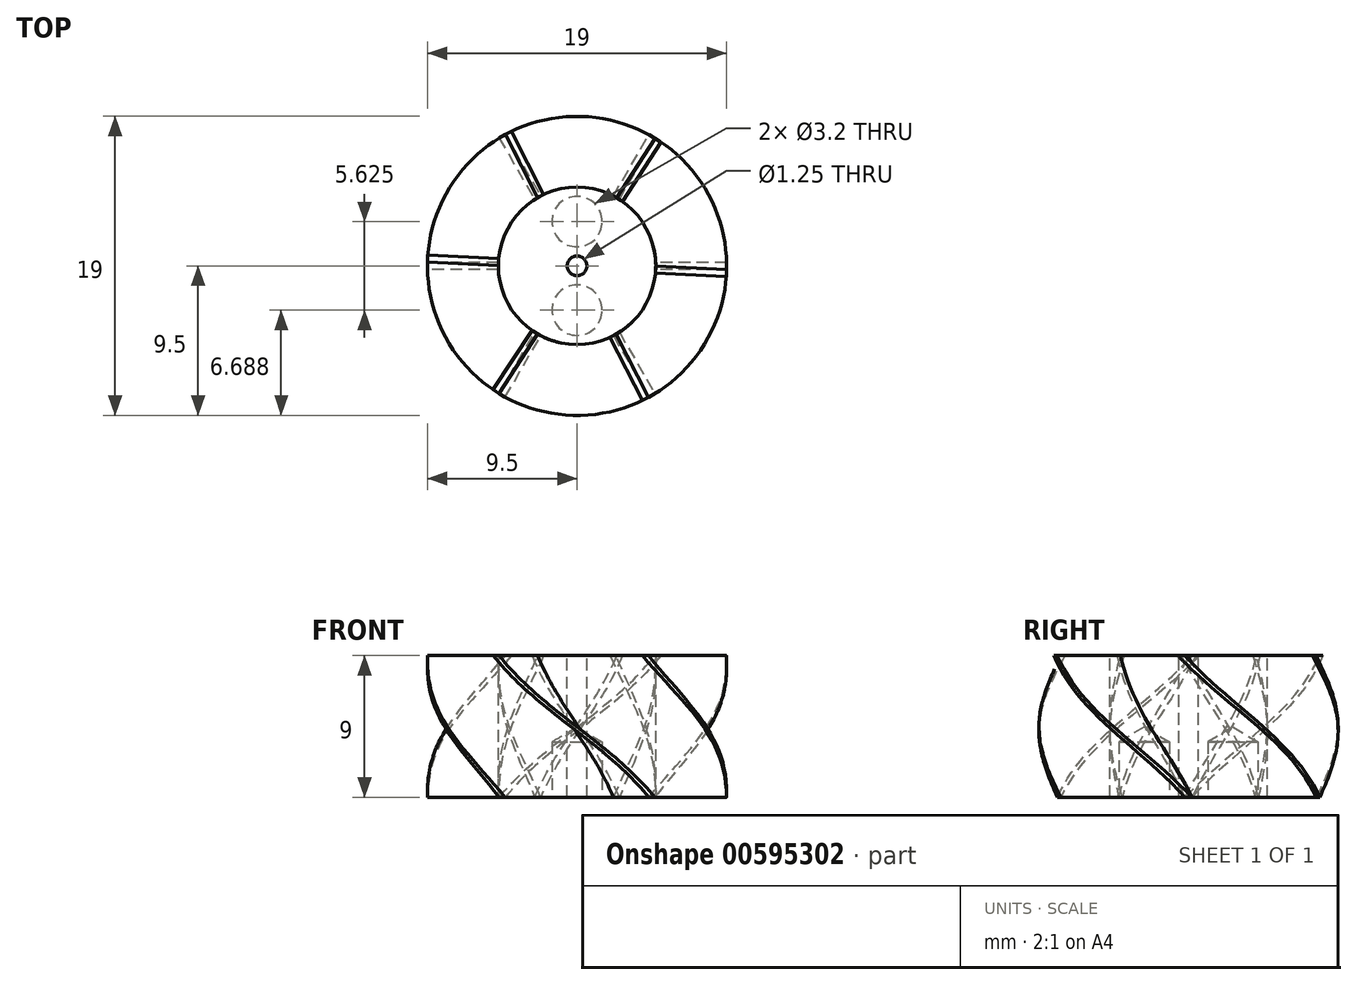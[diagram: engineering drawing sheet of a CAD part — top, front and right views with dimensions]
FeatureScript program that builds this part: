
annotation { "Feature Type Name" : "Feature", "Feature Type Description" : "" }
export const myFeature = defineFeature(function(context is Context, id is Id, definition is map)
    precondition{}
    {
        {
            var Q0;
            Q0=qCreatedBy(makeId("Top.planeOp"),FACE);
            var sketch = newSketch(context, id + "F0", { "sketchPlane" : qUnion([Q0])});
            skCircle(sketch, "E0", {"center": v(0, 0) * mm, "radius": 5 * mm});
            skLineSegment(sketch, "E1.bottom", {"start": v(13, -0.22) * mm, "end": v(5, -0.22) * mm});
            skLineSegment(sketch, "E1.top", {"start": v(13, 0.22) * mm, "end": v(5, 0.22) * mm});
            skLineSegment(sketch, "E1.left", {"start": v(13, -0.22) * mm, "end": v(13, 0.22) * mm});
            skLineSegment(sketch, "E1.right", {"start": v(-13, -0.22) * mm, "end": v(-13, 0.22) * mm});
            skLineSegment(sketch, "E2.1.0", {"start": v(-6.3, 11.36) * mm, "end": v(-6.69, 11.14) * mm});
            skLineSegment(sketch, "E2.1.1", {"start": v(6.69, -11.14) * mm, "end": v(6.3, -11.36) * mm});
            skLineSegment(sketch, "E2.1.2", {"start": v(-6.69, 11.14) * mm, "end": v(-2.69, 4.22) * mm});
            skLineSegment(sketch, "E2.1.3", {"start": v(-6.3, 11.36) * mm, "end": v(-2.3, 4.44) * mm});
            skLineSegment(sketch, "E2.2.0", {"start": v(-6.69, -11.14) * mm, "end": v(-6.3, -11.36) * mm});
            skLineSegment(sketch, "E2.2.1", {"start": v(6.3, 11.36) * mm, "end": v(6.69, 11.14) * mm});
            skLineSegment(sketch, "E2.2.2", {"start": v(-6.3, -11.36) * mm, "end": v(-2.3, -4.44) * mm});
            skLineSegment(sketch, "E2.2.3", {"start": v(-6.69, -11.14) * mm, "end": v(-2.69, -4.22) * mm});
            skLineSegment(sketch, "E3.trimOffspring", {"start": v(2.3, 4.44) * mm, "end": v(6.3, 11.36) * mm});
            skLineSegment(sketch, "E4.trimOffspring", {"start": v(2.69, 4.22) * mm, "end": v(6.69, 11.14) * mm});
            skLineSegment(sketch, "E5.trimOffspring", {"start": v(2.69, -4.22) * mm, "end": v(6.69, -11.14) * mm});
            skLineSegment(sketch, "E6.trimOffspring", {"start": v(-5, 0.22) * mm, "end": v(-13, 0.22) * mm});
            skLineSegment(sketch, "E7.trimOffspring", {"start": v(-5, -0.22) * mm, "end": v(-13, -0.22) * mm});
            skLineSegment(sketch, "E8.trimOffspring", {"start": v(2.3, -4.44) * mm, "end": v(6.3, -11.36) * mm});
            skCircle(sketch, "E9", {"center": v(0, 0) * mm, "radius": 0.62 * mm});
            skCircle(sketch, "E10", {"center": v(0, 2.81) * mm, "radius": 1.6 * mm});
            skCircle(sketch, "E11", {"center": v(0, -2.81) * mm, "radius": 1.6 * mm});
            skSolve(sketch);
        }
        {
            var Q0;
            Q0=qCreatedBy(makeId("Top.planeOp"),FACE);
            cPlane(context, id + "F1", {"entities" : qUnion([Q0]), "cplaneType" : CPlaneType.OFFSET, "offset" : 9 * mm, "width" : 150 * mm, "height" : 150 * mm});
        }
        {
            var Q0;
            Q0=qCreatedBy(id+"F1.planeOp",FACE);
            var sketch = newSketch(context, id + "F2", { "sketchPlane" : qUnion([Q0])});
            skCircle(sketch, "E12", {"center": v(0, 0) * mm, "radius": 5 * mm});
            skLineSegment(sketch, "E13.bottom", {"start": v(5.74, -11.66) * mm, "end": v(2.09, -4.54) * mm});
            skLineSegment(sketch, "E13.top", {"start": v(6.13, -11.46) * mm, "end": v(2.48, -4.34) * mm});
            skLineSegment(sketch, "E13.left", {"start": v(5.74, -11.66) * mm, "end": v(6.13, -11.46) * mm});
            skLineSegment(sketch, "E13.right", {"start": v(-6.13, 11.46) * mm, "end": v(-5.74, 11.66) * mm});
            skLineSegment(sketch, "E14.1.0", {"start": v(7.23, 10.8) * mm, "end": v(6.86, 11.04) * mm});
            skLineSegment(sketch, "E14.1.1", {"start": v(-6.86, -11.04) * mm, "end": v(-7.23, -10.8) * mm});
            skLineSegment(sketch, "E14.1.2", {"start": v(6.86, 11.04) * mm, "end": v(2.52, 4.32) * mm});
            skLineSegment(sketch, "E14.1.3", {"start": v(7.23, 10.8) * mm, "end": v(2.9, 4.08) * mm});
            skLineSegment(sketch, "E14.2.0", {"start": v(-12.97, 0.86) * mm, "end": v(-13, 0.42) * mm});
            skLineSegment(sketch, "E14.2.1", {"start": v(13, -0.42) * mm, "end": v(12.97, -0.86) * mm});
            skLineSegment(sketch, "E14.2.2", {"start": v(-13, 0.42) * mm, "end": v(-5, 0.03) * mm});
            skLineSegment(sketch, "E14.2.3", {"start": v(-12.97, 0.86) * mm, "end": v(-4.98, 0.47) * mm});
            skLineSegment(sketch, "E15.trimOffspring", {"start": v(5, -0.03) * mm, "end": v(13, -0.42) * mm});
            skLineSegment(sketch, "E16.trimOffspring", {"start": v(4.98, -0.47) * mm, "end": v(12.97, -0.86) * mm});
            skLineSegment(sketch, "E17.trimOffspring", {"start": v(-2.5, -4.33) * mm, "end": v(-6.86, -11.04) * mm});
            skLineSegment(sketch, "E18.trimOffspring", {"start": v(-2.11, 4.53) * mm, "end": v(-5.74, 11.66) * mm});
            skLineSegment(sketch, "E19.trimOffspring", {"start": v(-2.5, 4.33) * mm, "end": v(-6.13, 11.46) * mm});
            skLineSegment(sketch, "E20.trimOffspring", {"start": v(-2.87, -4.1) * mm, "end": v(-7.23, -10.8) * mm});
            skCircle(sketch, "E21", {"center": v(0, 0) * mm, "radius": 0.62 * mm});
            skSolve(sketch);
        }
        {
            var Q0;
            Q0=qCreatedBy(makeId("Top.planeOp"),FACE);
            cPlane(context, id + "F3", {"entities" : qUnion([Q0]), "cplaneType" : CPlaneType.OFFSET, "offset" : 5 * mm, "oppositeDirection" : true, "width" : 150 * mm, "height" : 150 * mm});
        }
        {
            var Q0;
            Q0=qCreatedBy(id+"F3.planeOp",FACE);
            var sketch = newSketch(context, id + "F4", { "sketchPlane" : qUnion([Q0])});
            skCircle(sketch, "E22", {"center": v(0, 0) * mm, "radius": 5 * mm});
            skCircle(sketch, "E23", {"center": v(0, 0) * mm, "radius": 9.5 * mm});
            skSolve(sketch);
        }
        {
            var Q0;
            Q0=makeQuery(id+"F2.imprint","IMPRINT",FACE,{"disambiguationData":[TD([[makeQuery(id+"F2.imprint","IMPRINT",EDGE,{"derivedFrom":sQuery(id+"F2.wireOp",EDGE,"E14.1.1")}),-1.0]])]});
            var Q1;
            Q1=makeQuery(id+"F0.imprint","IMPRINT",FACE,{"disambiguationData":[TD([[makeQuery(id+"F0.imprint","IMPRINT",EDGE,{"derivedFrom":sQuery(id+"F0.wireOp",EDGE,"E2.1.1")}),-1.0]])]});
            loft(context, id + "F5", {"sheetProfilesArray" : [{ "sheetProfileEntities" : qUnion([Q0]) }, { "sheetProfileEntities" : qUnion([Q1]) }]});
        }
        {
            var Q0;
            {var subQ0=sQuery(id+"F2.wireOp",EDGE,"E13.bottom");Q0=makeQuery(id+"F2.imprint","IMPRINT",FACE,{"disambiguationData":[TD([[makeQuery(id+"F2.imprint","IMPRINT",EDGE,{"derivedFrom":subQ0}),-1.0]])]});}
            var Q1;
            {var subQ0=sQuery(id+"F0.wireOp",EDGE,"E1.bottom");Q1=makeQuery(id+"F0.imprint","IMPRINT",FACE,{"disambiguationData":[TD([[makeQuery(id+"F0.imprint","IMPRINT",EDGE,{"derivedFrom":subQ0}),-1.0]])]});}
            loft(context, id + "F6", {"sheetProfilesArray" : [{ "sheetProfileEntities" : qUnion([Q0]) }, { "sheetProfileEntities" : qUnion([Q1]) }]});
        }
        {
            var Q0;
            Q0=makeQuery(id+"F2.imprint","IMPRINT",FACE,{"disambiguationData":[TD([[makeQuery(id+"F2.imprint","IMPRINT",EDGE,{"derivedFrom":sQuery(id+"F2.wireOp",EDGE,"E14.2.1")}),-1.0]])]});
            var Q1;
            Q1=makeQuery(id+"F0.imprint","IMPRINT",FACE,{"disambiguationData":[TD([[makeQuery(id+"F0.imprint","IMPRINT",EDGE,{"derivedFrom":sQuery(id+"F0.wireOp",EDGE,"E2.2.1")}),-1.0]])]});
            loft(context, id + "F7", {"sheetProfilesArray" : [{ "sheetProfileEntities" : qUnion([Q0]) }, { "sheetProfileEntities" : qUnion([Q1]) }]});
        }
        {
            var Q0;
            Q0=makeQuery(id+"F2.imprint","IMPRINT",FACE,{"disambiguationData":[TD([[makeQuery(id+"F2.imprint","IMPRINT",EDGE,{"derivedFrom":sQuery(id+"F2.wireOp",EDGE,"E14.1.0")}),1.0]])]});
            var Q1;
            Q1=makeQuery(id+"F0.imprint","IMPRINT",FACE,{"disambiguationData":[TD([[makeQuery(id+"F0.imprint","IMPRINT",EDGE,{"derivedFrom":sQuery(id+"F0.wireOp",EDGE,"E2.1.0")}),1.0]])]});
            loft(context, id + "F8", {"sheetProfilesArray" : [{ "sheetProfileEntities" : qUnion([Q0]) }, { "sheetProfileEntities" : qUnion([Q1]) }]});
        }
        {
            var Q0;
            Q0=makeQuery(id+"F2.imprint","IMPRINT",FACE,{"disambiguationData":[TD([[makeQuery(id+"F2.imprint","IMPRINT",EDGE,{"derivedFrom":sQuery(id+"F2.wireOp",EDGE,"E13.right")}),-1.0]])]});
            var Q1;
            Q1=makeQuery(id+"F0.imprint","IMPRINT",FACE,{"disambiguationData":[TD([[makeQuery(id+"F0.imprint","IMPRINT",EDGE,{"derivedFrom":sQuery(id+"F0.wireOp",EDGE,"E1.right")}),-1.0]])]});
            loft(context, id + "F9", {"sheetProfilesArray" : [{ "sheetProfileEntities" : qUnion([Q0]) }, { "sheetProfileEntities" : qUnion([Q1]) }]});
        }
        {
            var Q0;
            Q0=makeQuery(id+"F2.imprint","IMPRINT",FACE,{"disambiguationData":[TD([[makeQuery(id+"F2.imprint","IMPRINT",EDGE,{"derivedFrom":sQuery(id+"F2.wireOp",EDGE,"E14.2.0")}),1.0]])]});
            var Q1;
            Q1=makeQuery(id+"F0.imprint","IMPRINT",FACE,{"disambiguationData":[TD([[makeQuery(id+"F0.imprint","IMPRINT",EDGE,{"derivedFrom":sQuery(id+"F0.wireOp",EDGE,"E2.2.0")}),1.0]])]});
            loft(context, id + "F10", {"sheetProfilesArray" : [{ "sheetProfileEntities" : qUnion([Q0]) }, { "sheetProfileEntities" : qUnion([Q1]) }]});
        }
        {
            var Q0;
            Q0 = qSketchRegion(id + "F4", true);
            extrude(context, id + "F11", {"entities" : qUnion([Q0]), "depth" : 25 * mm, "offsetDistance" : 25 * mm});
        }
        {
            var Q0;
            Q0 = qSketchRegion(id + "F4", true);
            extrude(context, id + "F12", {"entities" : qUnion([Q0]), "depth" : 25 * mm, "offsetDistance" : 25 * mm});
        }
        {
            var Q0;
            Q0 = qSketchRegion(id + "F4", true);
            extrude(context, id + "F13", {"entities" : qUnion([Q0]), "depth" : 25 * mm, "offsetDistance" : 25 * mm});
        }
        {
            var Q0;
            Q0 = qSketchRegion(id + "F4", true);
            extrude(context, id + "F14", {"entities" : qUnion([Q0]), "depth" : 25 * mm, "offsetDistance" : 25 * mm});
        }
        {
            var Q0;
            Q0 = qSketchRegion(id + "F4", true);
            extrude(context, id + "F15", {"entities" : qUnion([Q0]), "depth" : 25 * mm, "offsetDistance" : 25 * mm});
        }
        {
            var Q0;
            Q0 = qSketchRegion(id + "F4", true);
            extrude(context, id + "F16", {"entities" : qUnion([Q0]), "depth" : 25 * mm, "offsetDistance" : 25 * mm});
        }
        {
            var Q0;
            Q0=makeQuery(id+"F5.opLoft","SWEPT_BODY",BODY,{"disambiguationData":[OSD([makeQuery(id+"F0.imprint","IMPRINT",FACE,{"disambiguationData":[TD([[makeQuery(id+"F0.imprint","IMPRINT",EDGE,{"derivedFrom":sQuery(id+"F0.wireOp",EDGE,"E2.1.1")}),-1.0]])]}),makeQuery(id+"F2.imprint","IMPRINT",FACE,{"disambiguationData":[TD([[makeQuery(id+"F2.imprint","IMPRINT",EDGE,{"derivedFrom":sQuery(id+"F2.wireOp",EDGE,"E14.1.1")}),-1.0]])]})])]});
            var Q1;
            Q1=makeQuery(id+"F11.opExtrude","SWEPT_BODY",BODY,{"disambiguationData":[OSD([sQuery(id+"F4.wireOp",EDGE,"E22"),sQuery(id+"F4.wireOp",EDGE,"E23")])]});
            booleanBodies(context, id + "F17", {"operationType" : BooleanOperationType.INTERSECTION, "tools" : qUnion([Q0, Q1])});
        }
        {
            var Q0;
            {var subQ0=sQuery(id+"F2.wireOp",EDGE,"E13.bottom");var subQ3=sQuery(id+"F0.wireOp",EDGE,"E1.bottom");Q0=makeQuery(id+"F6.opLoft","SWEPT_BODY",BODY,{"disambiguationData":[OSD([makeQuery(id+"F0.imprint","IMPRINT",FACE,{"disambiguationData":[TD([[makeQuery(id+"F0.imprint","IMPRINT",EDGE,{"derivedFrom":subQ3}),-1.0]])]}),makeQuery(id+"F2.imprint","IMPRINT",FACE,{"disambiguationData":[TD([[makeQuery(id+"F2.imprint","IMPRINT",EDGE,{"derivedFrom":subQ0}),-1.0]])]})])]});}
            var Q1;
            Q1=makeQuery(id+"F12.opExtrude","SWEPT_BODY",BODY,{"disambiguationData":[OSD([sQuery(id+"F4.wireOp",EDGE,"E22"),sQuery(id+"F4.wireOp",EDGE,"E23")])]});
            booleanBodies(context, id + "F18", {"operationType" : BooleanOperationType.INTERSECTION, "tools" : qUnion([Q0, Q1])});
        }
        {
            var Q0;
            Q0=makeQuery(id+"F7.opLoft","SWEPT_BODY",BODY,{"disambiguationData":[OSD([makeQuery(id+"F0.imprint","IMPRINT",FACE,{"disambiguationData":[TD([[makeQuery(id+"F0.imprint","IMPRINT",EDGE,{"derivedFrom":sQuery(id+"F0.wireOp",EDGE,"E2.2.1")}),-1.0]])]}),makeQuery(id+"F2.imprint","IMPRINT",FACE,{"disambiguationData":[TD([[makeQuery(id+"F2.imprint","IMPRINT",EDGE,{"derivedFrom":sQuery(id+"F2.wireOp",EDGE,"E14.2.1")}),-1.0]])]})])]});
            var Q1;
            Q1=makeQuery(id+"F13.opExtrude","SWEPT_BODY",BODY,{"disambiguationData":[OSD([sQuery(id+"F4.wireOp",EDGE,"E22"),sQuery(id+"F4.wireOp",EDGE,"E23")])]});
            booleanBodies(context, id + "F19", {"operationType" : BooleanOperationType.INTERSECTION, "tools" : qUnion([Q0, Q1])});
        }
        {
            var Q0;
            Q0=makeQuery(id+"F8.opLoft","SWEPT_BODY",BODY,{"disambiguationData":[OSD([makeQuery(id+"F0.imprint","IMPRINT",FACE,{"disambiguationData":[TD([[makeQuery(id+"F0.imprint","IMPRINT",EDGE,{"derivedFrom":sQuery(id+"F0.wireOp",EDGE,"E2.1.0")}),1.0]])]}),makeQuery(id+"F2.imprint","IMPRINT",FACE,{"disambiguationData":[TD([[makeQuery(id+"F2.imprint","IMPRINT",EDGE,{"derivedFrom":sQuery(id+"F2.wireOp",EDGE,"E14.1.0")}),1.0]])]})])]});
            var Q1;
            Q1=makeQuery(id+"F14.opExtrude","SWEPT_BODY",BODY,{"disambiguationData":[OSD([sQuery(id+"F4.wireOp",EDGE,"E22"),sQuery(id+"F4.wireOp",EDGE,"E23")])]});
            booleanBodies(context, id + "F20", {"operationType" : BooleanOperationType.INTERSECTION, "tools" : qUnion([Q0, Q1])});
        }
        {
            var Q0;
            Q0=makeQuery(id+"F9.opLoft","SWEPT_BODY",BODY,{"disambiguationData":[OSD([makeQuery(id+"F0.imprint","IMPRINT",FACE,{"disambiguationData":[TD([[makeQuery(id+"F0.imprint","IMPRINT",EDGE,{"derivedFrom":sQuery(id+"F0.wireOp",EDGE,"E1.right")}),-1.0]])]}),makeQuery(id+"F2.imprint","IMPRINT",FACE,{"disambiguationData":[TD([[makeQuery(id+"F2.imprint","IMPRINT",EDGE,{"derivedFrom":sQuery(id+"F2.wireOp",EDGE,"E13.right")}),-1.0]])]})])]});
            var Q1;
            Q1=makeQuery(id+"F15.opExtrude","SWEPT_BODY",BODY,{"disambiguationData":[OSD([sQuery(id+"F4.wireOp",EDGE,"E22"),sQuery(id+"F4.wireOp",EDGE,"E23")])]});
            booleanBodies(context, id + "F21", {"operationType" : BooleanOperationType.INTERSECTION, "tools" : qUnion([Q0, Q1])});
        }
        {
            var Q0;
            Q0=makeQuery(id+"F10.opLoft","SWEPT_BODY",BODY,{"disambiguationData":[OSD([makeQuery(id+"F0.imprint","IMPRINT",FACE,{"disambiguationData":[TD([[makeQuery(id+"F0.imprint","IMPRINT",EDGE,{"derivedFrom":sQuery(id+"F0.wireOp",EDGE,"E2.2.0")}),1.0]])]}),makeQuery(id+"F2.imprint","IMPRINT",FACE,{"disambiguationData":[TD([[makeQuery(id+"F2.imprint","IMPRINT",EDGE,{"derivedFrom":sQuery(id+"F2.wireOp",EDGE,"E14.2.0")}),1.0]])]})])]});
            var Q1;
            Q1=makeQuery(id+"F16.opExtrude","SWEPT_BODY",BODY,{"disambiguationData":[OSD([sQuery(id+"F4.wireOp",EDGE,"E22"),sQuery(id+"F4.wireOp",EDGE,"E23")])]});
            booleanBodies(context, id + "F22", {"operationType" : BooleanOperationType.INTERSECTION, "tools" : qUnion([Q0, Q1])});
        }
        {
            var Q0;
            Q0=makeQuery(id+"F2.imprint","IMPRINT",FACE,{"disambiguationData":[TD([[makeQuery(id+"F2.imprint","IMPRINT",EDGE,{"derivedFrom":sQuery(id+"F2.wireOp",EDGE,"E21")}),-1.0]])]});
            extrude(context, id + "F23", {"entities" : qUnion([Q0]), "oppositeDirection" : true, "depth" : 9 * mm, "offsetDistance" : 25 * mm});
        }
        {
            var Q0;
            Q0=makeQuery(id+"F0.imprint","IMPRINT",FACE,{"disambiguationData":[TD([[makeQuery(id+"F0.imprint","IMPRINT",EDGE,{"derivedFrom":sQuery(id+"F0.wireOp",EDGE,"E10")}),1.0]])]});
            extrude(context, id + "F24", {"entities" : qUnion([Q0]), "operationType" : NewBodyOperationType.ADD, "depth" : 3.5 * mm, "offsetDistance" : 25 * mm});
        }
        {
            var Q0;
            Q0=sQuery(id+"F0.wireOp",VERTEX,"E10.center");
            var Q1;
            Q1=makeQuery(id+"F23.opExtrude","SWEPT_BODY",BODY,{"disambiguationData":[OSD([sQuery(id+"F2.wireOp",EDGE,"E12"),sQuery(id+"F2.wireOp",EDGE,"E21")])]});
            hole(context, id + "F25", {"style" : HoleStyle.SIMPLE, "endStyle" : HoleEndStyle.BLIND, "oppositeDirection" : true, "holeDiameter" : 3.2 * mm, "majorDiameter" : 5 * mm, "holeDepth" : 3.5 * mm, "isTappedThrough" : true, "tappedDepth" : 12 * mm, "tapClearance" : 3, "locations" : qUnion([Q0]), "scope" : qUnion([Q1])});
        }
        {
            var Q0;
            Q0=sQuery(id+"F0.wireOp",VERTEX,"E11.center");
            var Q1;
            Q1=makeQuery(id+"F23.opExtrude","SWEPT_BODY",BODY,{"disambiguationData":[OSD([sQuery(id+"F2.wireOp",EDGE,"E12"),sQuery(id+"F2.wireOp",EDGE,"E21")])]});
            hole(context, id + "F26", {"style" : HoleStyle.SIMPLE, "endStyle" : HoleEndStyle.BLIND, "oppositeDirection" : true, "holeDiameter" : 3.2 * mm, "majorDiameter" : 5 * mm, "holeDepth" : 3.5 * mm, "isTappedThrough" : true, "tappedDepth" : 12 * mm, "tapClearance" : 3, "locations" : qUnion([Q0]), "scope" : qUnion([Q1])});
        }
    });
